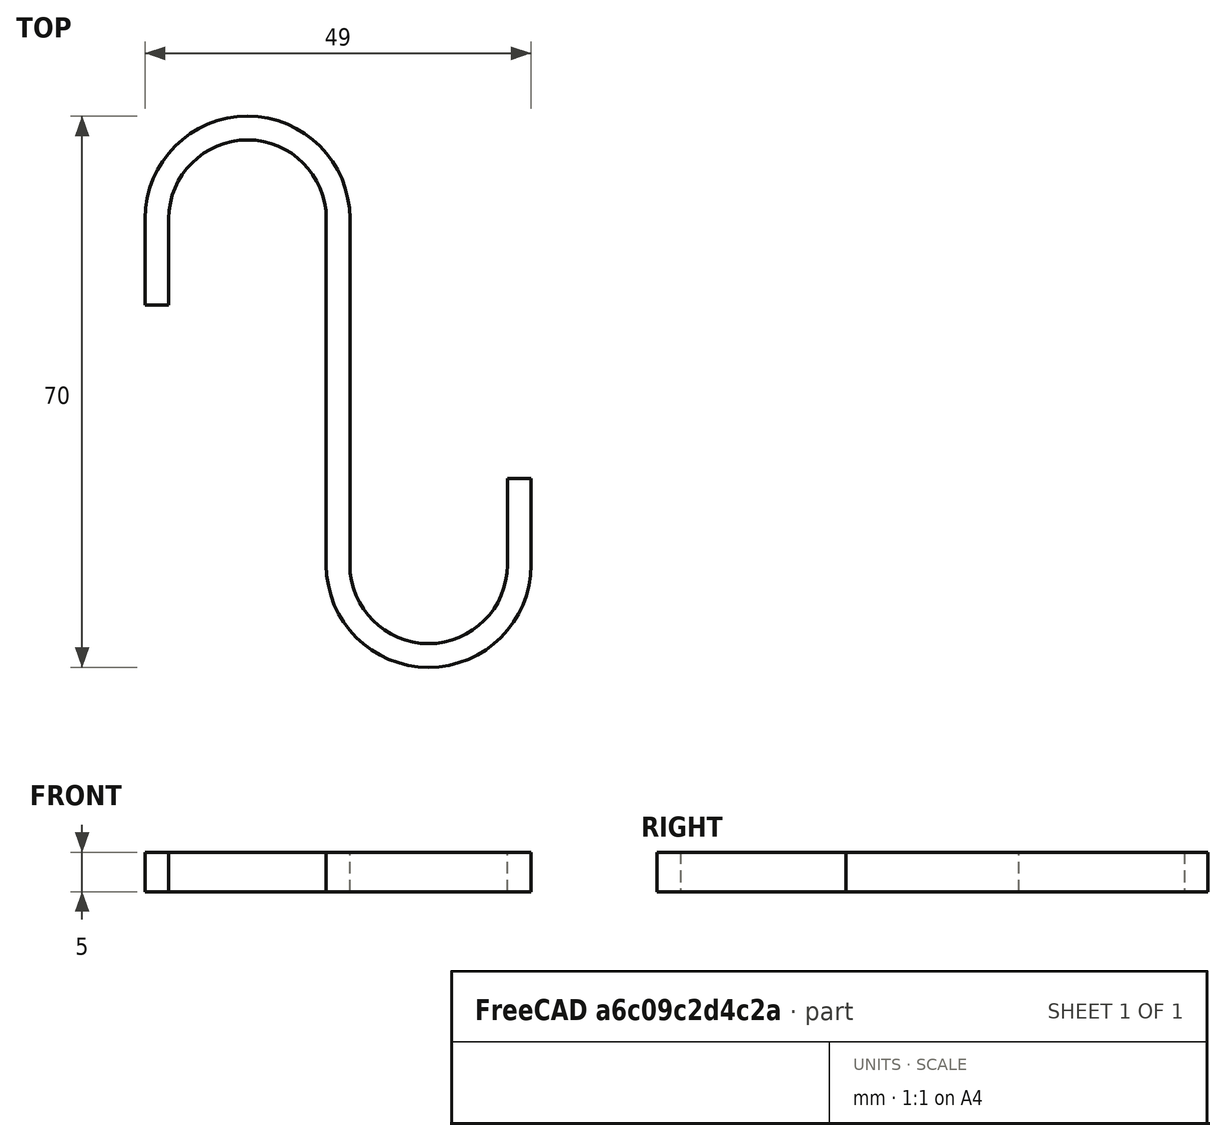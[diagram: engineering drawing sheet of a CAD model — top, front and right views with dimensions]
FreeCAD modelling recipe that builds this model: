
FCSTD DOCUMENT  (FreeCAD 0.16R6707 (Git))
Label: 12-01-Ikea-hook
License: All rights reserved
LicenseURL: http://en.wikipedia.org/wiki/All_rights_reserved
objects: Sketcher::SketchObject×1, PartDesign::Pad×1
note: 3 computed .brp shape members not serialized (recipe doc carries the construction recipe); baked Part::Feature solids carry a one-line shape summary decoded from their .brp

FEATURE [Sketcher::SketchObject] Sketch  label="hook-sketch"
  sketch-geometry (16):
    g0: LineSegment StartX=-1.5 StartY=22 StartZ=0 EndX=-1.5 EndY=-22 EndZ=0
    g1: LineSegment StartX=1.5 StartY=22 StartZ=0 EndX=1.5 EndY=-22 EndZ=0
    g2: LineSegment [constr] StartX=-21.5 StartY=22 StartZ=0 EndX=-1.5 EndY=22 EndZ=0
    g3: ArcOfCircle CenterX=-11.5 CenterY=22 CenterZ=0 NormalX=0 NormalY=0 NormalZ=1 Radius=10 StartAngle=0 EndAngle=3.14159
    g4: ArcOfCircle CenterX=-11.5 CenterY=22 CenterZ=0 NormalX=0 NormalY=0 NormalZ=1 Radius=13 StartAngle=0 EndAngle=3.14159
    g5: LineSegment [constr] StartX=1.5 StartY=-22 StartZ=0 EndX=21.5 EndY=-22 EndZ=0
    g6: ArcOfCircle CenterX=11.5 CenterY=-22 CenterZ=0 NormalX=0 NormalY=0 NormalZ=1 Radius=10 StartAngle=3.14159 EndAngle=6.28319
    g7: ArcOfCircle CenterX=11.5 CenterY=-22 CenterZ=0 NormalX=0 NormalY=0 NormalZ=1 Radius=13 StartAngle=3.14159 EndAngle=6.28319
    g8: LineSegment [constr] StartX=-11.5 StartY=35 StartZ=0 EndX=0 EndY=35 EndZ=0
    g9: LineSegment [constr] StartX=0 StartY=-35 StartZ=0 EndX=11.5 EndY=-35 EndZ=0
    g10: LineSegment StartX=-21.5 StartY=22 StartZ=0 EndX=-21.5 EndY=11 EndZ=0
    g11: LineSegment StartX=-21.5 StartY=11 StartZ=0 EndX=-24.5 EndY=11 EndZ=0
    g12: LineSegment StartX=-24.5 StartY=11 StartZ=0 EndX=-24.5 EndY=22 EndZ=0
    g13: LineSegment StartX=21.5 StartY=-11 StartZ=0 EndX=24.5 EndY=-11 EndZ=0
    g14: LineSegment StartX=24.5 StartY=-11 StartZ=0 EndX=24.5 EndY=-22 EndZ=0
    g15: LineSegment StartX=21.5 StartY=-22 StartZ=0 EndX=21.5 EndY=-11 EndZ=0
  constraints (48):
    c: Vertical(g0)
    c: Vertical(g1)
    c: Horizontal(g2)
    c: Coincident(g2,g0)
    c: PointOnObject(g3,g2)
    c: Coincident(g3,g2)
    c: Coincident(g3,g0)
    c: Coincident(g4,g3)
    c: Coincident(g4,g1)
    c: PointOnObject(g1,g2)
    c: Symmetric(g0,g1,g-2)
    c: Symmetric(g0,g0,g-1)
    c: Horizontal(g5)
    c: Coincident(g1,g5)
    c: Equal(g2,g5)
    c: PointOnObject(g6,g5)
    c: Coincident(g6,g5)
    c: Coincident(g6,g1)
    c: Coincident(g7,g6)
    c: Coincident(g7,g0)
    c: PointOnObject(g0,g5)
    c: Radius(g3) = 10
    c: Horizontal(g8)
    c: Tangent(g8,g4) = 1.5708
    c: PointOnObject(g8,g-2)
    c: Horizontal(g9)
    c: Tangent(g9,g7) = -1.5708
    c: PointOnObject(g9,g-2)
    c: DistanceY(g9,g8) = 70
    c: Coincident(g10,g11)
    c: Coincident(g11,g12)
    c: Horizontal(g11)
    c: Vertical(g10)
    c: Vertical(g12)
    c: Coincident(g12,g4)
    c: Coincident(g10,g2)
    c: PointOnObject(g4,g2)
    c: DistanceY(g12,g12) = 11
    c: DistanceX(g11,g11) = 3
    c: Coincident(g13,g14)
    c: Coincident(g15,g13)
    c: Horizontal(g13)
    c: Vertical(g14)
    c: Vertical(g15)
    c: Coincident(g15,g5)
    c: Coincident(g14,g7)
    c: PointOnObject(g7,g5)
    c: Equal(g15,g10)
FEATURE [PartDesign::Pad] Pad  label="Ikea-hook"
  Length = 5
  Length2 = 100
  Sketch = -> Sketch
  Type = 0
